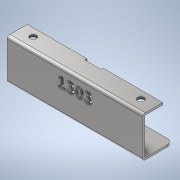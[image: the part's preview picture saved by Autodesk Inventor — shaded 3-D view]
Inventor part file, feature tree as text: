
AUTODESK INVENTOR PART (.ipt)
format: ipt  version: 2020 (Build 240168000, 168)  size: 514,560 bytes
history: native  units: mm
features: other x4, extrude x3, fillet x1, sketch x1, projected_geometry x1
ambient origin geometry x8: Origin, YZ Plane, XZ Plane, XY Plane, X Axis, Y Axis, Z Axis, Center Point
bodies: Body1 (feature_tree)
feature tree (10):
  other  "實體1"
  extrude  "擠出1"  Depth=125.7mm
  extrude  "擠出3"  Depth=26.3mm
  extrude  "擠出4"  Depth=33.0mm
  other  "折彎零件1"
  other  "折彎零件2"
  fillet  "圓角1"  Radius=17.0mm
  sketch  "草圖4"
  projected_geometry  "投影迴路1"
  other  "定義1"
